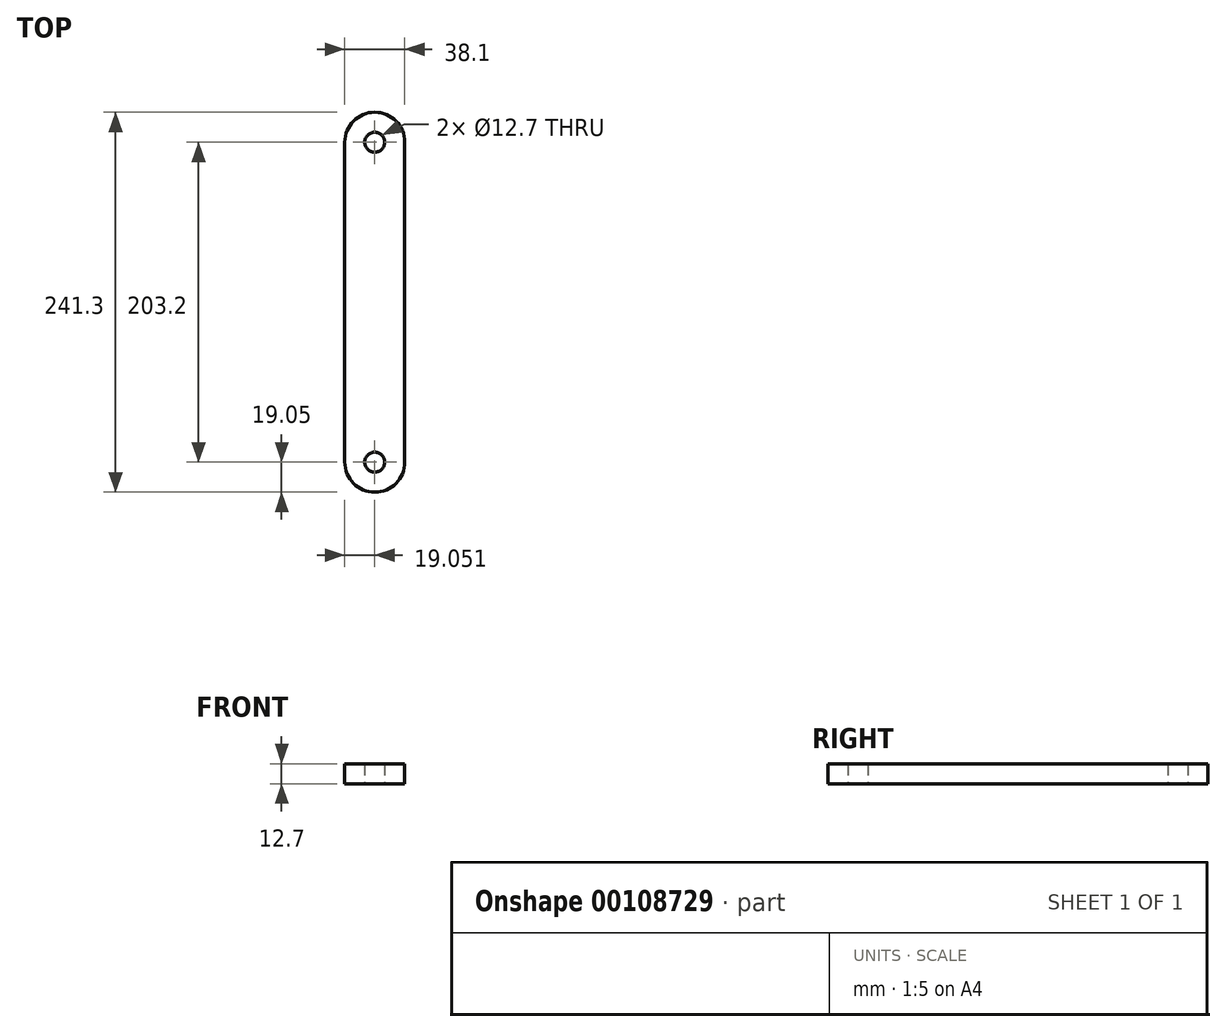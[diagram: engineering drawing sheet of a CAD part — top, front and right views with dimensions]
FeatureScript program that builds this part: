
annotation { "Feature Type Name" : "Feature", "Feature Type Description" : "" }
export const myFeature = defineFeature(function(context is Context, id is Id, definition is map)
    precondition{}
    {
        {
            var Q0;
            Q0=qCreatedBy(makeId("Top.planeOp"),FACE);
            var sketch = newSketch(context, id + "F0", { "sketchPlane" : qUnion([Q0])});
            skLineSegment(sketch, "E0.left", {"start": v(-33.96, 101.6) * mm, "end": v(-33.96, 0) * mm});
            skLineSegment(sketch, "E0.right", {"start": v(4.14, 101.6) * mm, "end": v(4.14, 0) * mm});
            skArc(sketch, "E1", {"start": v(4.14, 101.6) * mm, "mid": v(-14.9, 120.65) * mm, "end": v(-33.96, 101.6) * mm});
            skCircle(sketch, "E2", {"center": v(-14.9, 101.6) * mm, "radius": 6.35 * mm});
            skLineSegment(sketch, "E3.MirrorCS", {"start": v(-33.96, -101.6) * mm, "end": v(-33.96, 0) * mm});
            skArc(sketch, "E4.MirrorCS", {"start": v(4.14, -101.6) * mm, "mid": v(-14.9, -120.65) * mm, "end": v(-33.96, -101.6) * mm});
            skCircle(sketch, "E5.MirrorC", {"center": v(-14.9, -101.6) * mm, "radius": 6.35 * mm});
            skLineSegment(sketch, "E6.MirrorCS", {"start": v(4.14, -101.6) * mm, "end": v(4.14, 0) * mm});
            skSolve(sketch);
        }
        {
            var Q0;
            Q0 = qSketchRegion(id + "F0", true);
            extrude(context, id + "F1", {"entities" : qUnion([Q0]), "depth" : 12.7 * mm});
        }
    });
